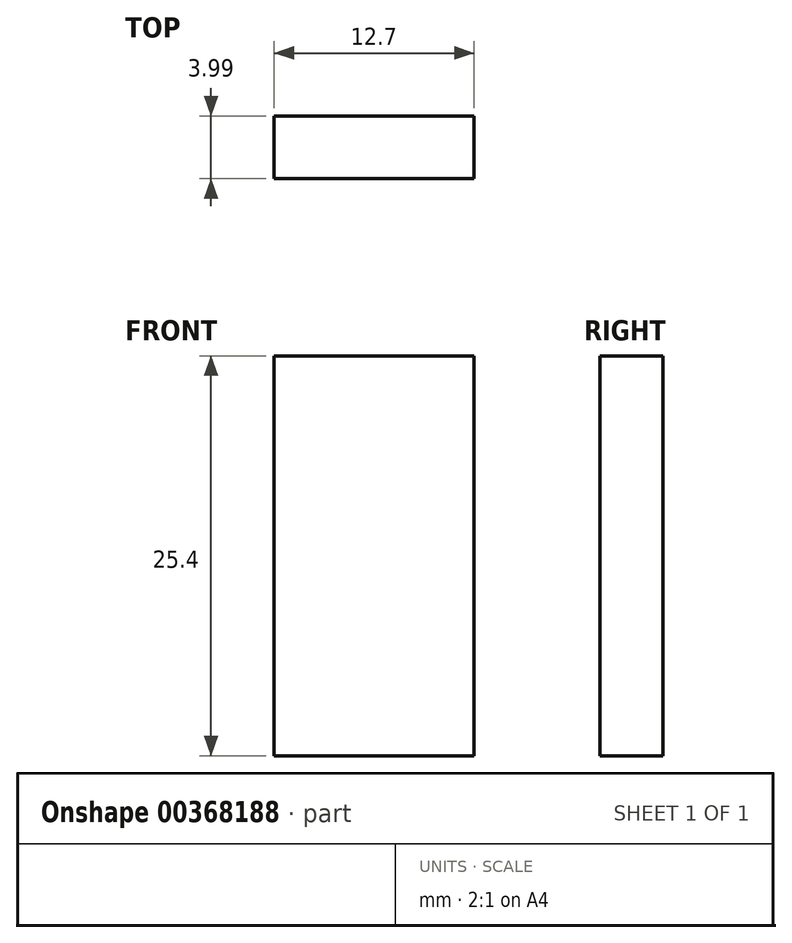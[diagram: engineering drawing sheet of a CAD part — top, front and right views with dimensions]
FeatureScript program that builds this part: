
annotation { "Feature Type Name" : "Feature", "Feature Type Description" : "" }
export const myFeature = defineFeature(function(context is Context, id is Id, definition is map)
    precondition{}
    {
        {
            var Q0;
            Q0=qCreatedBy(makeId("Front.planeOp"),FACE);
            var sketch = newSketch(context, id + "F0", { "sketchPlane" : qUnion([Q0])});
            skLineSegment(sketch, "E0.bottom", {"start": v(6.35, 12.7) * mm, "end": v(-6.35, 12.7) * mm});
            skLineSegment(sketch, "E0.top", {"start": v(6.35, -12.7) * mm, "end": v(-6.35, -12.7) * mm});
            skLineSegment(sketch, "E0.left", {"start": v(6.35, 12.7) * mm, "end": v(6.35, -12.7) * mm});
            skLineSegment(sketch, "E0.right", {"start": v(-6.35, 12.7) * mm, "end": v(-6.35, -12.7) * mm});
            skPoint(sketch, "E0.middle", {"position": v(0, 0) * mm});
            skSolve(sketch);
        }
        {
            var Q0;
            Q0=makeQuery(id+"F0.imprint","IMPRINT",FACE,{"disambiguationData":[TD([[makeQuery(id+"F0.imprint","IMPRINT",EDGE,{"derivedFrom":sQuery(id+"F0.wireOp",EDGE,"E0.bottom")}),1.0]])]});
            extrude(context, id + "F1", {"entities" : qUnion([Q0]), "depth" : 4 * mm});
        }
    });
